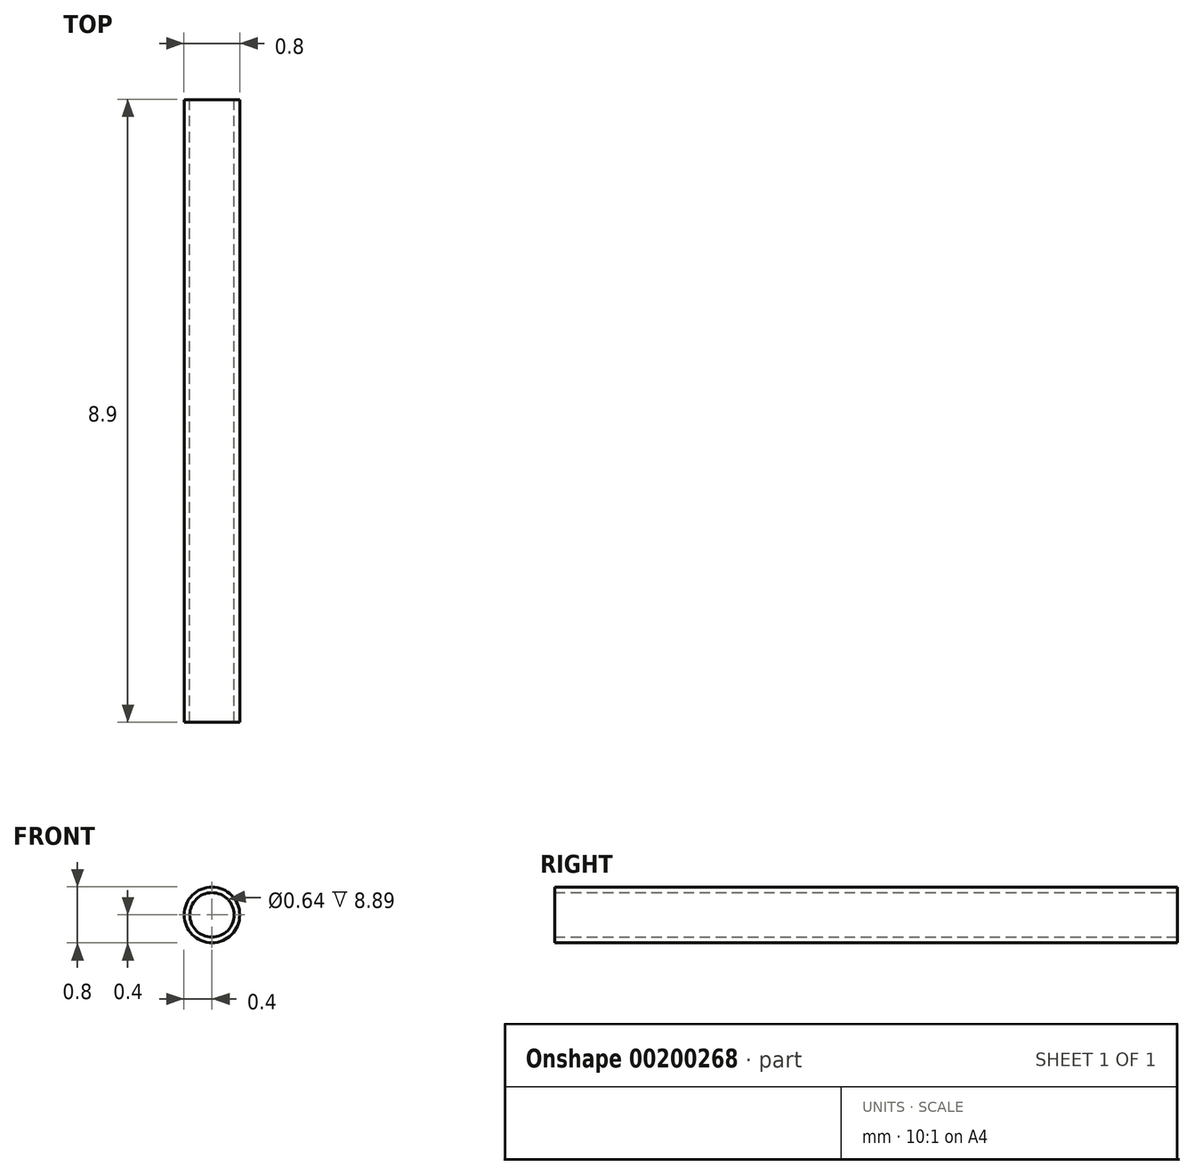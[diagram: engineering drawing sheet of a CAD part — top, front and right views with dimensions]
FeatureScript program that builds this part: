
annotation { "Feature Type Name" : "Feature", "Feature Type Description" : "" }
export const myFeature = defineFeature(function(context is Context, id is Id, definition is map)
    precondition{}
    {
        {
            var Q0;
            Q0=qCreatedBy(makeId("Front.planeOp"),FACE);
            var sketch = newSketch(context, id + "F0", { "sketchPlane" : qUnion([Q0])});
            skCircle(sketch, "E0", {"center": v(0, 0) * mm, "radius": 0.4 * mm});
            skCircle(sketch, "E1", {"center": v(0, 0) * mm, "radius": 0.32 * mm});
            skSolve(sketch);
        }
        {
            var Q0;
            Q0=makeQuery(id+"F0.imprint","IMPRINT",FACE,{"disambiguationData":[TD([[makeQuery(id+"F0.imprint","IMPRINT",EDGE,{"derivedFrom":sQuery(id+"F0.wireOp",EDGE,"E0")}),1.0]])]});
            extrude(context, id + "F1", {"entities" : qUnion([Q0]), "endBound" : BoundingType.SYMMETRIC, "depth" : 8.9 * mm, "offsetDistance" : 25.4 * mm});
        }
    });
